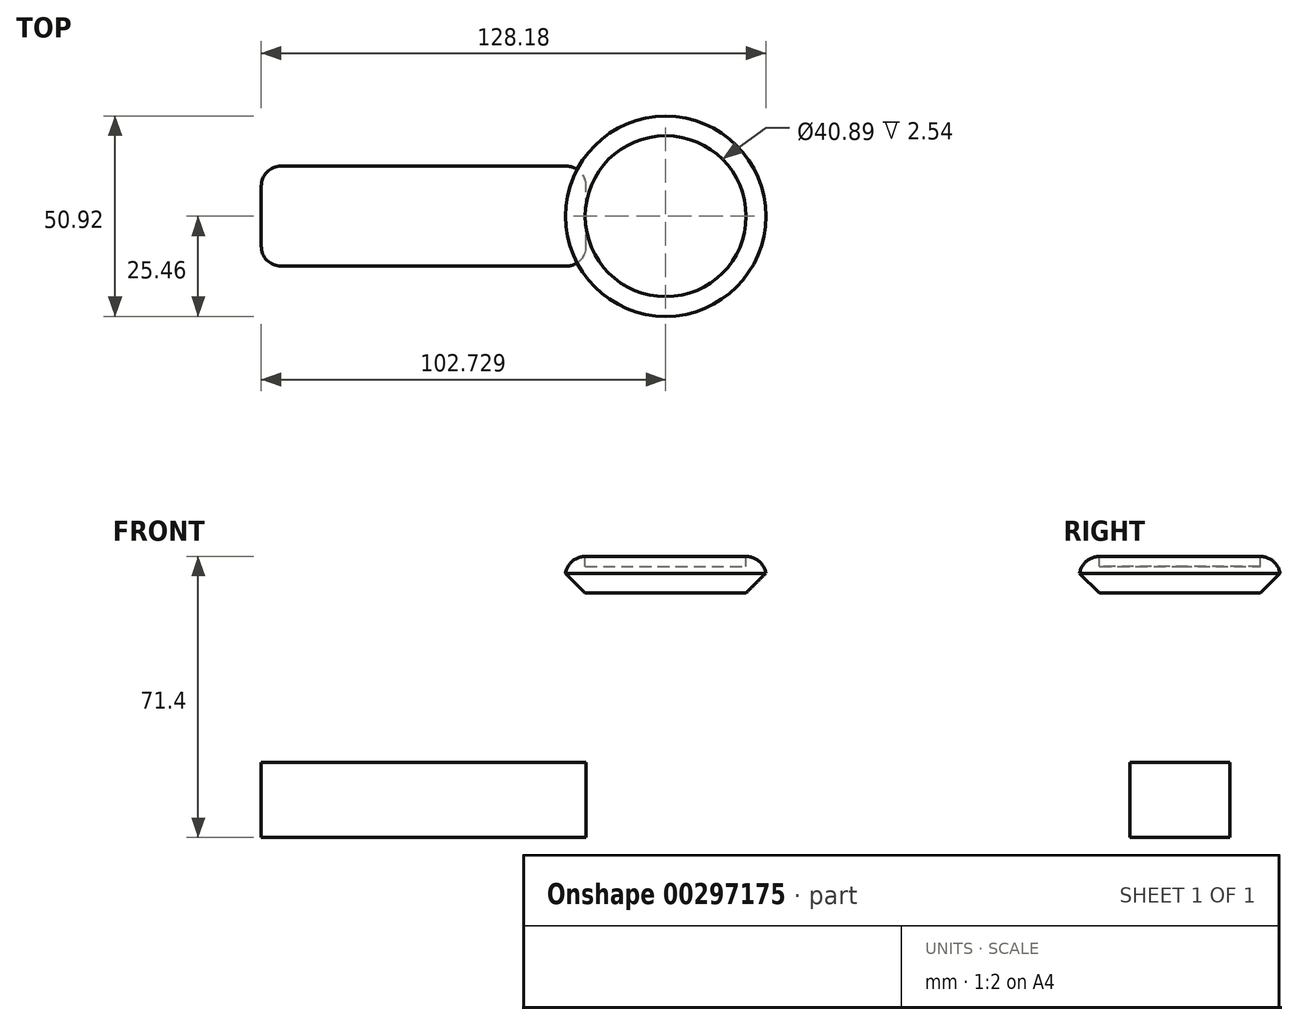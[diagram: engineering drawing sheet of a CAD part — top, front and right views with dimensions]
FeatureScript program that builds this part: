
annotation { "Feature Type Name" : "Feature", "Feature Type Description" : "" }
export const myFeature = defineFeature(function(context is Context, id is Id, definition is map)
    precondition{}
    {
        {
            var Q0;
            Q0=qCreatedBy(makeId("Front.planeOp"),FACE);
            var sketch = newSketch(context, id + "F0", { "sketchPlane" : qUnion([Q0])});
            skLineSegment(sketch, "E0.bottom", {"start": v(41.28, -9.52) * mm, "end": v(-41.28, -9.53) * mm});
            skLineSegment(sketch, "E0.top", {"start": v(41.28, 9.53) * mm, "end": v(-41.28, 9.52) * mm});
            skLineSegment(sketch, "E0.left", {"start": v(41.28, -9.52) * mm, "end": v(41.28, 9.53) * mm});
            skLineSegment(sketch, "E0.right", {"start": v(-41.28, -9.53) * mm, "end": v(-41.28, 9.52) * mm});
            skPoint(sketch, "E0.middle", {"position": v(0, 0) * mm});
            skLineSegment(sketch, "E1.bottom", {"start": v(50.81, 52.6) * mm, "end": v(17.14, 52.6) * mm});
            skLineSegment(sketch, "E1.top", {"start": v(50.81, 25.18) * mm, "end": v(17.14, 25.18) * mm});
            skLineSegment(sketch, "E1.left", {"start": v(50.81, 52.6) * mm, "end": v(50.81, 25.18) * mm});
            skLineSegment(sketch, "E1.right", {"start": v(17.14, 52.6) * mm, "end": v(17.14, 25.18) * mm});
            skPoint(sketch, "E1.middle", {"position": v(33.97, 38.9) * mm});
            skLineSegment(sketch, "E2", {"start": v(41.28, 9.53) * mm, "end": v(41.28, 18.04) * mm});
            skArc(sketch, "E3", {"start": v(41.28, 18.04) * mm, "mid": v(43.54, 23.57) * mm, "end": v(49.02, 25.94) * mm});
            skLineSegment(sketch, "E4", {"start": v(49.02, 25.94) * mm, "end": v(71.1, 25.94) * mm});
            skArc(sketch, "E5.0", {"start": v(-4.44, 18.04) * mm, "mid": v(10.9, 55.6) * mm, "end": v(48.15, 71.65) * mm});
            skFitSpline(sketch, "E6", {"points": [v(-41.28, 9.52) * mm, v(-4.44, 18.04) * mm], "startDerivative": vector(36.83, 8.52) * mm, "endDerivative": vector(36.83, 8.52) * mm});
            skLineSegment(sketch, "E7.bottom", {"start": v(35.94, 61.87) * mm, "end": v(61.46, 61.87) * mm});
            skLineSegment(sketch, "E7.top", {"start": v(35.94, 46.55) * mm, "end": v(61.46, 46.55) * mm});
            skLineSegment(sketch, "E7.left", {"start": v(35.94, 61.87) * mm, "end": v(35.94, 46.55) * mm});
            skLineSegment(sketch, "E7.right", {"start": v(61.46, 61.87) * mm, "end": v(61.46, 46.55) * mm});
            skLineSegment(sketch, "E8", {"start": v(50.81, 52.6) * mm, "end": v(61.46, 52.6) * mm});
            skSolve(sketch);
        }
        {
            var Q0;
            Q0=makeQuery(id+"F0.imprint","IMPRINT",FACE,{"disambiguationData":[TD([[makeQuery(id+"F0.imprint","IMPRINT",EDGE,{"derivedFrom":sQuery(id+"F0.wireOp",EDGE,"E0.bottom")}),-1.0]])]});
            extrude(context, id + "F1", {"entities" : qUnion([Q0]), "endBound" : BoundingType.SYMMETRIC, "depth" : 25.4 * mm});
        }
        {
            var Q0;
            {var subQ1=sQuery(id+"F0.wireOp",EDGE,"E7.bottom");Q0=makeQuery(id+"F0.imprint","IMPRINT",FACE,{"disambiguationData":[TD([[makeQuery(id+"F0.imprint","IMPRINT",EDGE,{"derivedFrom":subQ1}),-1.0]])]});}
            var Q1;
            Q1=sQuery(id+"F0.wireOp",EDGE,"E7.right");
            revolve(context, id + "F2", {"entities" : qUnion([Q0]), "axis" : qUnion([Q1]), "revolveType" : RevolveType.FULL});
        }
        {
            var Q0;
            Q0=makeQuery(id+"F1.opExtrude","CAP_EDGE",EDGE,{"disambiguationData":[OSD([sQuery(id+"F0.wireOp",EDGE,"E0.right")])],"isStart":false});
            var Q1;
            Q1=makeQuery(id+"F1.opExtrude","CAP_EDGE",EDGE,{"disambiguationData":[OSD([sQuery(id+"F0.wireOp",EDGE,"E0.left")])],"isStart":false});
            var Q2;
            Q2=makeQuery(id+"F1.opExtrude","CAP_EDGE",EDGE,{"disambiguationData":[OSD([sQuery(id+"F0.wireOp",EDGE,"E0.left")])],"isStart":true});
            var Q3;
            Q3=makeQuery(id+"F1.opExtrude","CAP_EDGE",EDGE,{"disambiguationData":[OSD([sQuery(id+"F0.wireOp",EDGE,"E0.right")])],"isStart":true});
            fillet(context, id + "F3", {"entities" : qUnion([Q0, Q1, Q2, Q3]), "radius" : 5.08 * mm, "tangentPropagation" : true, "allowEdgeOverflow" : false});
        }
        {
            var Q0;
            Q0=makeQuery(id+"F2.opRevolve","SWEPT_EDGE",EDGE,{"disambiguationData":[OSD([sQuery(id+"F0.wireOp",EDGE,"E7.bottom"),sQuery(id+"F0.wireOp",EDGE,"E7.left")])]});
            fillet(context, id + "F4", {"entities" : qUnion([Q0]), "radius" : 5.08 * mm, "tangentPropagation" : true, "allowEdgeOverflow" : false});
        }
        {
            var Q0;
            Q0=makeQuery(id+"F2.opRevolve","SWEPT_EDGE",EDGE,{"disambiguationData":[OSD([sQuery(id+"F0.wireOp",EDGE,"E1.bottom"),sQuery(id+"F0.wireOp",EDGE,"E7.left")])]});
            chamfer(context, id + "F5", {"entities" : qUnion([Q0]), "width" : 5.08 * mm, "tangentPropagation" : true});
        }
        {
            var Q0;
            Q0=makeQuery(id+"F2.opRevolve","SWEPT_FACE",FACE,{"disambiguationData":[OSD([sQuery(id+"F0.wireOp",EDGE,"E7.bottom")])]});
            extrude(context, id + "F6", {"entities" : qUnion([Q0]), "operationType" : NewBodyOperationType.REMOVE, "oppositeDirection" : true, "depth" : 2.54 * mm});
        }
    });
